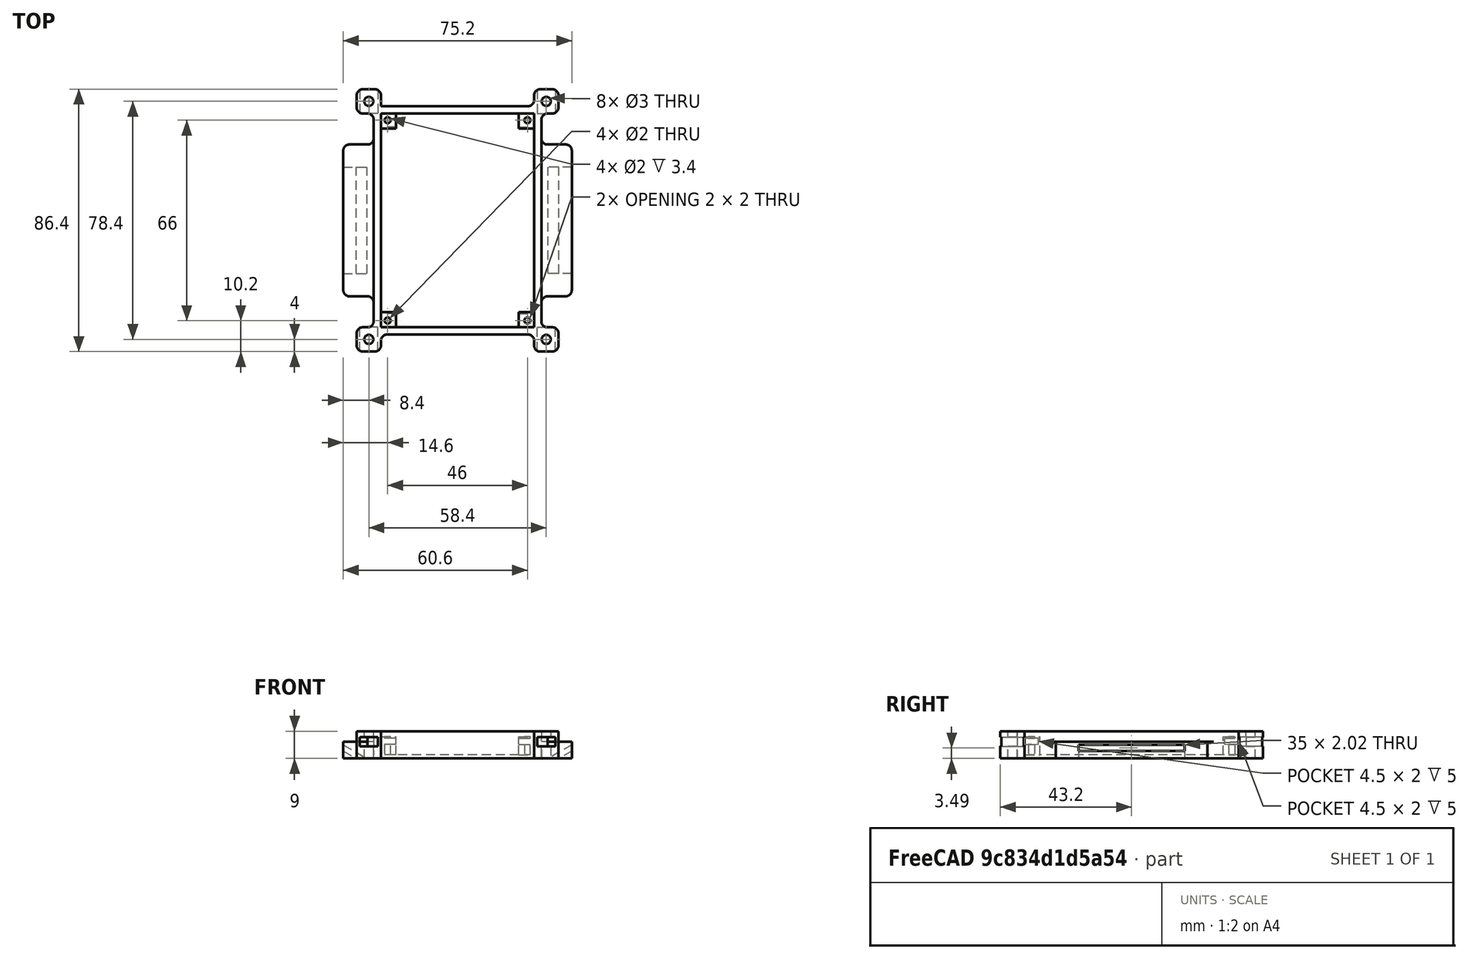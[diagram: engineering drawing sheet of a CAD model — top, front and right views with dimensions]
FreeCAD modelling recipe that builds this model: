
FCSTD DOCUMENT  (FreeCAD 0.20R29410 (Git))
Label: baseplate-2
License: All rights reserved
LicenseURL: http://en.wikipedia.org/wiki/All_rights_reserved
objects: Sketcher::SketchObject×12, PartDesign::Pad×6, PartDesign::Pocket×5, PartDesign::Fillet×3, PartDesign::Mirrored×2, Spreadsheet::Sheet×1, PartDesign::Body×1
note: 43 computed .brp shape members not serialized (recipe doc carries the construction recipe); baked Part::Feature solids carry a one-line shape summary decoded from their .brp

FEATURE [Sketcher::SketchObject] Sketch
  FullyConstrained = true
  MapMode = 5
  Support = -> [XY_Plane]
  expr: Constraints[34] = 50 + Spreadsheet.clc * 2
  expr: Constraints[35] = 70 + Spreadsheet.clc * 2
  expr: Constraints[46] = 50 + 2 * Spreadsheet.clc + 2 * Spreadsheet.thk
  expr: Constraints[47] = 70 + 2 * Spreadsheet.clc + 2 * Spreadsheet.thk
  sketch-geometry (35):
    g0: LineSegment StartX=25 StartY=35 StartZ=0 EndX=25 EndY=-35 EndZ=0
    g1: LineSegment StartX=25 StartY=-35 StartZ=0 EndX=-25 EndY=-35 EndZ=0
    g2: LineSegment StartX=-25 StartY=-35 StartZ=0 EndX=-25 EndY=35 EndZ=0
    g3: LineSegment StartX=-25 StartY=35 StartZ=0 EndX=25 EndY=35 EndZ=0
    g4: GeomPoint X=0 Y=0 Z=0
    g5: Circle CenterX=-23 CenterY=33 CenterZ=0 NormalX=0 NormalY=0 NormalZ=1 AngleXU=0 Radius=1
    g6: Circle CenterX=23 CenterY=33 CenterZ=0 NormalX=0 NormalY=0 NormalZ=1 AngleXU=0 Radius=1
    g7: Circle CenterX=23 CenterY=-33 CenterZ=0 NormalX=0 NormalY=0 NormalZ=1 AngleXU=0 Radius=1
    g8: Circle CenterX=-23 CenterY=-33 CenterZ=0 NormalX=0 NormalY=0 NormalZ=1 AngleXU=0 Radius=1
    g9: LineSegment StartX=-25.2 StartY=-35.2 StartZ=0 EndX=-25.2 EndY=35.2 EndZ=0
    g10: LineSegment StartX=-25.2 StartY=35.2 StartZ=0 EndX=25.2 EndY=35.2 EndZ=0
    g11: LineSegment StartX=25.2 StartY=35.2 StartZ=0 EndX=25.2 EndY=-35.2 EndZ=0
    g12: LineSegment StartX=25.2 StartY=-35.2 StartZ=0 EndX=-25.2 EndY=-35.2 EndZ=0
    g13: GeomPoint X=0 Y=0 Z=0
    g14: LineSegment StartX=-27.6 StartY=37.6 StartZ=0 EndX=-27.6 EndY=-37.6 EndZ=0
    g15: LineSegment StartX=-27.6 StartY=-37.6 StartZ=0 EndX=27.6 EndY=-37.6 EndZ=0
    g16: LineSegment StartX=27.6 StartY=-37.6 StartZ=0 EndX=27.6 EndY=37.6 EndZ=0
    g17: LineSegment StartX=27.6 StartY=37.6 StartZ=0 EndX=-27.6 EndY=37.6 EndZ=0
    g18: GeomPoint X=0 Y=0 Z=0
    g19: LineSegment StartX=25.2 StartY=35.2 StartZ=0 EndX=20.2 EndY=35.2 EndZ=0
    g20: LineSegment StartX=20.2 StartY=35.2 StartZ=0 EndX=20.2 EndY=30.2 EndZ=0
    g21: LineSegment StartX=20.2 StartY=30.2 StartZ=0 EndX=25.2 EndY=30.2 EndZ=0
    g22: LineSegment StartX=25.2 StartY=30.2 StartZ=0 EndX=25.2 EndY=35.2 EndZ=0
    g23: LineSegment StartX=25.2 StartY=-35.2 StartZ=0 EndX=20.2 EndY=-35.2 EndZ=0
    g24: LineSegment StartX=20.2 StartY=-35.2 StartZ=0 EndX=20.2 EndY=-30.2 EndZ=0
    g25: LineSegment StartX=20.2 StartY=-30.2 StartZ=0 EndX=25.2 EndY=-30.2 EndZ=0
    g26: LineSegment StartX=25.2 StartY=-30.2 StartZ=0 EndX=25.2 EndY=-35.2 EndZ=0
    g27: LineSegment StartX=-25.2 StartY=-35.2 StartZ=0 EndX=-20.2 EndY=-35.2 EndZ=0
    g28: LineSegment StartX=-20.2 StartY=-35.2 StartZ=0 EndX=-20.2 EndY=-30.2 EndZ=0
    g29: LineSegment StartX=-20.2 StartY=-30.2 StartZ=0 EndX=-25.2 EndY=-30.2 EndZ=0
    g30: LineSegment StartX=-25.2 StartY=-30.2 StartZ=0 EndX=-25.2 EndY=-35.2 EndZ=0
    g31: LineSegment StartX=-25.2 StartY=35.2 StartZ=0 EndX=-20.2 EndY=35.2 EndZ=0
    g32: LineSegment StartX=-20.2 StartY=35.2 StartZ=0 EndX=-20.2 EndY=30.2 EndZ=0
    g33: LineSegment StartX=-20.2 StartY=30.2 StartZ=0 EndX=-25.2 EndY=30.2 EndZ=0
    g34: LineSegment StartX=-25.2 StartY=30.2 StartZ=0 EndX=-25.2 EndY=35.2 EndZ=0
  constraints (92):
    c: Coincident(g0,g1)
    c: Coincident(g1,g2)
    c: Coincident(g2,g3)
    c: Coincident(g3,g0)
    c: Horizontal(g1)
    c: Horizontal(g3)
    c: Vertical(g0)
    c: Vertical(g2)
    c: Symmetric(g1,g0,g4)
    c: Coincident(g4,g-1)
    c: Diameter(g5) = 2
    c: Equal(g5,g6)
    c: Equal(g6,g7)
    c: Equal(g7,g8)
    c: DistanceX(g2,g5) = 2
    c: DistanceY(g5,g2) = 2
    c: DistanceY(g0,g7) = 2
    c: DistanceX(g7,g0) = 2
    c: Horizontal(g8,g7)
    c: Horizontal(g6,g5)
    c: Vertical(g8,g5)
    c: Vertical(g7,g6)
    c: DistanceX(g3,g3) = 50
    c: DistanceY(g2,g2) = 70
    c: Coincident(g9,g10)
    c: Coincident(g10,g11)
    c: Coincident(g11,g12)
    c: Coincident(g12,g9)
    c: Horizontal(g10)
    c: Horizontal(g12)
    c: Vertical(g9)
    c: Vertical(g11)
    c: Symmetric(g10,g9,g13)
    c: Coincident(g13,g4)
    c: DistanceX(g10,g10) = 50.4
    c: DistanceY(g11,g11) = 70.4
    c: Coincident(g14,g15)
    c: Coincident(g15,g16)
    c: Coincident(g16,g17)
    c: Coincident(g17,g14)
    c: Horizontal(g15)
    c: Horizontal(g17)
    c: Vertical(g14)
    c: Vertical(g16)
    c: Symmetric(g15,g14,g18)
    c: Coincident(g18,g4)
    c: DistanceX(g17,g17) = 55.2
    c: DistanceY(g16,g16) = 75.2
    c: Coincident(g19,g20)
    c: Coincident(g20,g21)
    c: Coincident(g21,g22)
    c: Coincident(g22,g19)
    c: Horizontal(g19)
    c: Horizontal(g21)
    c: Vertical(g20)
    c: Vertical(g22)
    c: Coincident(g19,g10)
    c: DistanceY(g20,g20) = 5
    c: Coincident(g23,g24)
    c: Coincident(g24,g25)
    c: Coincident(g25,g26)
    c: Coincident(g26,g23)
    c: Horizontal(g23)
    c: Horizontal(g25)
    c: Vertical(g24)
    c: Vertical(g26)
    c: Coincident(g23,g11)
    c: Coincident(g27,g28)
    c: Coincident(g28,g29)
    c: Coincident(g29,g30)
    c: Coincident(g30,g27)
    c: Horizontal(g27)
    c: Horizontal(g29)
    c: Vertical(g28)
    c: Vertical(g30)
    c: Coincident(g27,g9)
    c: Coincident(g31,g32)
    c: Coincident(g32,g33)
    c: Coincident(g33,g34)
    c: Coincident(g34,g31)
    c: Horizontal(g31)
    c: Horizontal(g33)
    c: Vertical(g32)
    c: Vertical(g34)
    c: Coincident(g31,g9)
    c: Equal(g21,g20)
    c: Equal(g33,g32)
    c: Equal(g32,g29)
    c: Equal(g29,g28)
    c: Equal(g28,g24)
    c: Equal(g24,g25)
    c: Equal(g32,g21)
FEATURE [Spreadsheet::Sheet] Spreadsheet
  cells = A1=clearance; B1(clc)=0.2; A2=thk; B2(thk)=2.4
FEATURE [PartDesign::Pad] Pad
  Direction = (0,0,1)
  Length = 1.2
  Length2 = 10
  Profile = -> Sketch
  ReferenceAxis = -> Sketch [N_Axis]
  Type = 0
  expr: Length = Spreadsheet.thk / 2
FEATURE [Sketcher::SketchObject] Sketch001
  FullyConstrained = true
  MapMode = 5
  Placement = pos=(0,0,1.2) rot=(0,0,1;0rad)
  Support = -> [Pad]
  expr: Constraints[1] = Sketch.Constraints[10]
  expr: Constraints[24] = Sketch.Constraints[46]
  expr: Constraints[25] = Sketch.Constraints[47]
  expr: Constraints[29] = Sketch.Constraints[57]
  expr: Constraints[50] = Spreadsheet.thk
  expr: Constraints[51] = Spreadsheet.thk
  expr: Constraints[52] = Spreadsheet.thk
  expr: Constraints[53] = Spreadsheet.thk
  expr: Constraints[56] = 2.8mm
  sketch-geometry (23):
    g0: GeomPoint X=0 Y=0 Z=0
    g1: Circle CenterX=-23 CenterY=33 CenterZ=0 NormalX=0 NormalY=0 NormalZ=1 AngleXU=0 Radius=1
    g2: Circle CenterX=23 CenterY=33 CenterZ=0 NormalX=0 NormalY=0 NormalZ=1 AngleXU=0 Radius=1
    g3: Circle CenterX=23 CenterY=-33 CenterZ=0 NormalX=0 NormalY=0 NormalZ=1 AngleXU=0 Radius=1
    g4: Circle CenterX=-23 CenterY=-33 CenterZ=0 NormalX=0 NormalY=0 NormalZ=1 AngleXU=0 Radius=1
    g5: LineSegment StartX=-25.2 StartY=-30.2 StartZ=0 EndX=-25.2 EndY=30.2 EndZ=0
    g6: LineSegment StartX=-20.2 StartY=35.2 StartZ=0 EndX=20.2 EndY=35.2 EndZ=0
    g7: LineSegment StartX=25.2 StartY=30.2 StartZ=0 EndX=25.2 EndY=-30.2 EndZ=0
    g8: LineSegment StartX=20.2 StartY=-35.2 StartZ=0 EndX=-20.2 EndY=-35.2 EndZ=0
    g9: GeomPoint X=0 Y=0 Z=0
    g10: LineSegment StartX=-27.6 StartY=37.6 StartZ=0 EndX=-27.6 EndY=-37.6 EndZ=0
    g11: LineSegment StartX=-27.6 StartY=-37.6 StartZ=0 EndX=27.6 EndY=-37.6 EndZ=0
    g12: LineSegment StartX=27.6 StartY=-37.6 StartZ=0 EndX=27.6 EndY=37.6 EndZ=0
    g13: LineSegment StartX=27.6 StartY=37.6 StartZ=0 EndX=-27.6 EndY=37.6 EndZ=0
    g14: GeomPoint X=0 Y=0 Z=0
    g15: LineSegment StartX=20.2 StartY=35.2 StartZ=0 EndX=20.2 EndY=30.2 EndZ=0
    g16: LineSegment StartX=20.2 StartY=30.2 StartZ=0 EndX=25.2 EndY=30.2 EndZ=0
    g17: LineSegment StartX=20.2 StartY=-35.2 StartZ=0 EndX=20.2 EndY=-30.2 EndZ=0
    g18: LineSegment StartX=20.2 StartY=-30.2 StartZ=0 EndX=25.2 EndY=-30.2 EndZ=0
    g19: LineSegment StartX=-20.2 StartY=-35.2 StartZ=0 EndX=-20.2 EndY=-30.2 EndZ=0
    g20: LineSegment StartX=-20.2 StartY=-30.2 StartZ=0 EndX=-25.2 EndY=-30.2 EndZ=0
    g21: LineSegment StartX=-20.2 StartY=35.2 StartZ=0 EndX=-20.2 EndY=30.2 EndZ=0
    g22: LineSegment StartX=-20.2 StartY=30.2 StartZ=0 EndX=-25.2 EndY=30.2 EndZ=0
  constraints (68):
    c: Coincident(g0,g-1)
    c: Diameter(g1) = 2
    c: Equal(g1,g2)
    c: Equal(g2,g3)
    c: Equal(g3,g4)
    c: Horizontal(g4,g3)
    c: Horizontal(g2,g1)
    c: Vertical(g4,g1)
    c: Vertical(g3,g2)
    c: Horizontal(g6)
    c: Horizontal(g8)
    c: Vertical(g5)
    c: Vertical(g7)
    c: Coincident(g9,g0)
    c: Coincident(g10,g11)
    c: Coincident(g11,g12)
    c: Coincident(g12,g13)
    c: Coincident(g13,g10)
    c: Horizontal(g11)
    c: Horizontal(g13)
    c: Vertical(g10)
    c: Vertical(g12)
    c: Symmetric(g11,g10,g14)
    c: Coincident(g14,g0)
    c: DistanceX(g13,g13) = 55.2
    c: DistanceY(g12,g12) = 75.2
    c: Coincident(g15,g16)
    c: Horizontal(g16)
    c: Vertical(g15)
    c: DistanceY(g15,g15) = 5
    c: Coincident(g17,g18)
    c: Horizontal(g18)
    c: Vertical(g17)
    c: Coincident(g19,g20)
    c: Horizontal(g20)
    c: Vertical(g19)
    c: Coincident(g21,g22)
    c: Horizontal(g22)
    c: Vertical(g21)
    c: Equal(g16,g15)
    c: Equal(g22,g21)
    c: Equal(g21,g20)
    c: Equal(g20,g19)
    c: Equal(g19,g17)
    c: Equal(g17,g18)
    c: Equal(g21,g16)
    c: PointOnObject(g7,g18)
    c: PointOnObject(g5,g20)
    c: PointOnObject(g5,g22)
    c: PointOnObject(g7,g16)
    c: DistanceY(g11,g8) = 2.4
    c: DistanceX(g7,g11) = 2.4
    c: DistanceX(g10,g5) = 2.4
    c: DistanceY(g6,g10) = 2.4
    c: Equal(g6,g8)
    c: Equal(g7,g5)
    c: DistanceX(g6,g2) = 2.8
    c: DistanceY(g15,g2) = 2.8
    c: DistanceY(g8,g4) = 2.2
    c: DistanceX(g5,g4) = 2.2
    c: DistanceX(g10,g21) = 7.4
    c: DistanceX(g17,g11) = 7.4
    c: DistanceY(g21,g10) = 7.4
    c: DistanceX(g6,g12) = 7.4
    c: DistanceX(g10,g19) = 7.4
    c: Coincident(g8,g17)
    c: Coincident(g8,g19)
    c: Coincident(g16,g7)
FEATURE [PartDesign::Pad] Pad001
  BaseFeature = -> Pad
  Direction = (0,0,1)
  Length = 6
  Length2 = 10
  Profile = -> Sketch001
  ReferenceAxis = -> Sketch001 [N_Axis]
  Type = 0
FEATURE [Sketcher::SketchObject] Sketch002
  ExternalGeometry = -> [Pad001]
  FullyConstrained = true
  MapMode = 5
  Placement = pos=(0,0,7.2) rot=(0,0,1;0rad)
  Support = -> [Pad001]
  expr: Constraints[20] = 50 + Spreadsheet.clc * 2
  expr: Constraints[21] = 70 + Spreadsheet.clc * 2
  sketch-geometry (9):
    g0: LineSegment StartX=-27.6 StartY=37.6 StartZ=0 EndX=27.6 EndY=37.6 EndZ=0
    g1: LineSegment StartX=27.6 StartY=37.6 StartZ=0 EndX=27.6 EndY=-37.6 EndZ=0
    g2: LineSegment StartX=27.6 StartY=-37.6 StartZ=0 EndX=-27.6 EndY=-37.6 EndZ=0
    g3: LineSegment StartX=-27.6 StartY=-37.6 StartZ=0 EndX=-27.6 EndY=37.6 EndZ=0
    g4: LineSegment StartX=-25.2 StartY=35.2 StartZ=0 EndX=-25.2 EndY=-35.2 EndZ=0
    g5: LineSegment StartX=-25.2 StartY=-35.2 StartZ=0 EndX=25.2 EndY=-35.2 EndZ=0
    g6: LineSegment StartX=25.2 StartY=-35.2 StartZ=0 EndX=25.2 EndY=35.2 EndZ=0
    g7: LineSegment StartX=25.2 StartY=35.2 StartZ=0 EndX=-25.2 EndY=35.2 EndZ=0
    g8: GeomPoint X=0 Y=0 Z=0
  constraints (22):
    c: Coincident(g0,g1)
    c: Coincident(g1,g2)
    c: Coincident(g2,g3)
    c: Coincident(g3,g0)
    c: Horizontal(g0)
    c: Horizontal(g2)
    c: Vertical(g1)
    c: Vertical(g3)
    c: Coincident(g0,g-3)
    c: Coincident(g1,g-4)
    c: Coincident(g4,g5)
    c: Coincident(g5,g6)
    c: Coincident(g6,g7)
    c: Coincident(g7,g4)
    c: Horizontal(g5)
    c: Horizontal(g7)
    c: Vertical(g4)
    c: Vertical(g6)
    c: Symmetric(g5,g4,g8)
    c: Coincident(g8,g-1)
    c: DistanceX(g7,g7) = 50.4
    c: DistanceY(g6,g6) = 70.4
FEATURE [PartDesign::Pad] Pad002
  BaseFeature = -> Pad001
  Direction = (0,0,1)
  Length = 9.8
  Length2 = 10
  Profile = -> Sketch002
  ReferenceAxis = -> Sketch002 [N_Axis]
  Type = 0
FEATURE [Sketcher::SketchObject] Sketch003
  ExternalGeometry = -> [Pad002]
  FullyConstrained = true
  MapMode = 5
  Placement = pos=(0,0,17) rot=(0,0,1;0rad)
  Support = -> [Pad002]
  sketch-geometry (16):
    g0: LineSegment StartX=25.2 StartY=-35.2 StartZ=0 EndX=33.2 EndY=-35.2 EndZ=0
    g1: LineSegment StartX=33.2 StartY=-35.2 StartZ=0 EndX=33.2 EndY=-43.2 EndZ=0
    g2: LineSegment StartX=33.2 StartY=-43.2 StartZ=0 EndX=25.2 EndY=-43.2 EndZ=0
    g3: LineSegment StartX=25.2 StartY=-43.2 StartZ=0 EndX=25.2 EndY=-35.2 EndZ=0
    g4: LineSegment StartX=-25.2 StartY=-35.2 StartZ=0 EndX=-33.2 EndY=-35.2 EndZ=0
    g5: LineSegment StartX=-33.2 StartY=-35.2 StartZ=0 EndX=-33.2 EndY=-43.2 EndZ=0
    g6: LineSegment StartX=-33.2 StartY=-43.2 StartZ=0 EndX=-25.2 EndY=-43.2 EndZ=0
    g7: LineSegment StartX=-25.2 StartY=-43.2 StartZ=0 EndX=-25.2 EndY=-35.2 EndZ=0
    g8: LineSegment StartX=-25.2 StartY=35.2 StartZ=0 EndX=-33.2 EndY=35.2 EndZ=0
    g9: LineSegment StartX=-33.2 StartY=35.2 StartZ=0 EndX=-33.2 EndY=43.2 EndZ=0
    g10: LineSegment StartX=-33.2 StartY=43.2 StartZ=0 EndX=-25.2 EndY=43.2 EndZ=0
    g11: LineSegment StartX=-25.2 StartY=43.2 StartZ=0 EndX=-25.2 EndY=35.2 EndZ=0
    g12: LineSegment StartX=25.2 StartY=35.2 StartZ=0 EndX=33.2 EndY=35.2 EndZ=0
    g13: LineSegment StartX=33.2 StartY=35.2 StartZ=0 EndX=33.2 EndY=43.2 EndZ=0
    g14: LineSegment StartX=33.2 StartY=43.2 StartZ=0 EndX=25.2 EndY=43.2 EndZ=0
    g15: LineSegment StartX=25.2 StartY=43.2 StartZ=0 EndX=25.2 EndY=35.2 EndZ=0
  constraints (44):
    c: Coincident(g0,g1)
    c: Coincident(g1,g2)
    c: Coincident(g2,g3)
    c: Coincident(g3,g0)
    c: Horizontal(g0)
    c: Horizontal(g2)
    c: Vertical(g1)
    c: Vertical(g3)
    c: Coincident(g0,g-6)
    c: Coincident(g4,g5)
    c: Coincident(g5,g6)
    c: Coincident(g6,g7)
    c: Coincident(g7,g4)
    c: Horizontal(g4)
    c: Horizontal(g6)
    c: Vertical(g5)
    c: Vertical(g7)
    c: Coincident(g4,g-5)
    c: Coincident(g8,g9)
    c: Coincident(g9,g10)
    c: Coincident(g10,g11)
    c: Coincident(g11,g8)
    c: Horizontal(g8)
    c: Horizontal(g10)
    c: Vertical(g9)
    c: Vertical(g11)
    c: Coincident(g8,g-4)
    c: Coincident(g12,g13)
    c: Coincident(g13,g14)
    c: Coincident(g14,g15)
    c: Coincident(g15,g12)
    c: Horizontal(g12)
    c: Horizontal(g14)
    c: Vertical(g13)
    c: Vertical(g15)
    c: Coincident(g12,g-3)
    c: Equal(g10,g9)
    c: Equal(g9,g14)
    c: Equal(g14,g13)
    c: Equal(g13,g1)
    c: Equal(g1,g2)
    c: Equal(g2,g6)
    c: Equal(g6,g5)
    c: DistanceY(g13,g13) = 8
FEATURE [PartDesign::Pad] Pad003
  BaseFeature = -> Pad002
  Direction = (0,0,1)
  Length = 10
  Length2 = 10
  Profile = -> Sketch003
  ReferenceAxis = -> Sketch003 [N_Axis]
  Reversed = true
  Type = 3
  UpToFace = -> Pad002 [Face4]
FEATURE [PartDesign::Fillet] Fillet
  Base = -> Pad003 [Edge79,Edge78,Edge41,Edge21,Edge20,Edge27,Edge51,Edge53,Edge33,Edge60,Edge102,Edge65,Edge67,Edge66,Edge71,Edge69,Edge73,Edge38,Edge108,Edge80,Edge84,Edge82,Edge43,Edge86,Edge114,Edge91,Edge54,Edge57,Edge46,Edge30,Edge29,Edge28]
  BaseFeature = -> Pad003
  Radius = 2
  SupportTransform = false
  UseAllEdges = false
  expr: Radius = 2
FEATURE [Sketcher::SketchObject] Sketch004
  ExternalGeometry = -> [Fillet]
  FullyConstrained = true
  MapMode = 5
  Placement = pos=(-20.2,0,0) rot=(0.57735,0.57735,0.57735;2.0944rad)
  Support = -> [Fillet]
  sketch-geometry (8):
    g0: LineSegment StartX=30.7 StartY=6.6 StartZ=0 EndX=35.2 EndY=6.6 EndZ=0
    g1: LineSegment StartX=35.2 StartY=6.6 StartZ=0 EndX=35.2 EndY=4.6 EndZ=0
    g2: LineSegment StartX=35.2 StartY=4.6 StartZ=0 EndX=30.7 EndY=4.6 EndZ=0
    g3: LineSegment StartX=30.7 StartY=4.6 StartZ=0 EndX=30.7 EndY=6.6 EndZ=0
    g4: LineSegment StartX=-30.7 StartY=6.6 StartZ=0 EndX=-35.2 EndY=6.6 EndZ=0
    g5: LineSegment StartX=-35.2 StartY=6.6 StartZ=0 EndX=-35.2 EndY=4.6 EndZ=0
    g6: LineSegment StartX=-35.2 StartY=4.6 StartZ=0 EndX=-30.7 EndY=4.6 EndZ=0
    g7: LineSegment StartX=-30.7 StartY=4.6 StartZ=0 EndX=-30.7 EndY=6.6 EndZ=0
  constraints (24):
    c: Coincident(g0,g1)
    c: Coincident(g1,g2)
    c: Coincident(g2,g3)
    c: Coincident(g3,g0)
    c: Horizontal(g0)
    c: Horizontal(g2)
    c: Vertical(g1)
    c: Vertical(g3)
    c: DistanceY(g3,g3) = 2
    c: DistanceX(g0,g0) = 4.5
    c: DistanceX(g-3,g0) = 0.5
    c: Coincident(g4,g5)
    c: Coincident(g5,g6)
    c: Coincident(g6,g7)
    c: Coincident(g7,g4)
    c: Horizontal(g4)
    c: Horizontal(g6)
    c: Vertical(g5)
    c: Vertical(g7)
    c: DistanceX(g4,g4) = 4.5
    c: DistanceX(g4,g-4) = 0.5
    c: DistanceY(g7,g7) = 2
    c: PointOnObject(g2,g6)
    c: DistanceY(g4,g-4) = 0.6
FEATURE [PartDesign::Pocket] Pocket
  BaseFeature = -> Fillet
  Direction = (-1,0,0)
  Length = 0
  Length2 = 5
  Profile = -> Sketch004
  ReferenceAxis = -> Sketch004 [N_Axis]
  Type = 3
  UpToFace = -> Fillet [Face85]
FEATURE [PartDesign::Mirrored] Mirrored
  BaseFeature = -> Pocket
  MirrorPlane = -> YZ_Plane
  Originals = -> [Pocket]
FEATURE [Sketcher::SketchObject] Sketch005
  FullyConstrained = true
  MapMode = 5
  Placement = pos=(0,-43.2,0) rot=(1,0,0;1.5708rad)
  Support = -> [Mirrored]
FEATURE [Sketcher::SketchObject] Sketch006
  ExternalGeometry = -> [Mirrored]
  FullyConstrained = false
  MapMode = 5
  Placement = pos=(0,0,17) rot=(0,0,1;0rad)
  Support = -> [Mirrored]
  sketch-geometry (8):
    g0: Circle CenterX=-29.2 CenterY=39.2 CenterZ=0 NormalX=0 NormalY=0 NormalZ=1 AngleXU=0 Radius=1.5
    g1: Circle CenterX=29.2 CenterY=39.2 CenterZ=0 NormalX=0 NormalY=0 NormalZ=1 AngleXU=0 Radius=1.5
    g2: Circle CenterX=29.2 CenterY=-39.2 CenterZ=0 NormalX=0 NormalY=0 NormalZ=1 AngleXU=0 Radius=1.5
    g3: Circle CenterX=-29.2 CenterY=-39.2 CenterZ=0 NormalX=0 NormalY=0 NormalZ=1 AngleXU=0 Radius=1.5
    g4: LineSegment StartX=29.2 StartY=-39.2 StartZ=0 EndX=29.2 EndY=-42.1749 EndZ=0
    g5: LineSegment StartX=29.2 StartY=-39.2 StartZ=0 EndX=32.2991 EndY=-39.2 EndZ=0
    g6: LineSegment StartX=-29.2 StartY=39.2 StartZ=0 EndX=-29.2 EndY=42.4001 EndZ=0
    g7: LineSegment StartX=-29.2 StartY=39.2 StartZ=0 EndX=-32.1259 EndY=39.2 EndZ=0
  constraints (16):
    c: Equal(g0,g1)
    c: Equal(g1,g2)
    c: Equal(g2,g3)
    c: Diameter(g0) = 3
    c: Coincident(g4,g2)
    c: Symmetric(g-5,g-5,g4)
    c: Symmetric(g-6,g-6,g5)
    c: Coincident(g2,g5)
    c: Coincident(g6,g0)
    c: Coincident(g7,g0)
    c: Symmetric(g-3,g-3,g6)
    c: Symmetric(g-4,g-4,g7)
    c: Horizontal(g1,g0)
    c: Horizontal(g2,g3)
    c: Vertical(g3,g0)
    c: Vertical(g1,g2)
FEATURE [PartDesign::Pocket] Pocket001
  BaseFeature = -> Mirrored
  Direction = (0,0,-1)
  Length = 5
  Length2 = 5
  Profile = -> Sketch006
  ReferenceAxis = -> Sketch006 [N_Axis]
  Type = 1
FEATURE [Sketcher::SketchObject] Sketch007
  ExternalGeometry = -> [Pocket001]
  FullyConstrained = false
  MapMode = 5
  Placement = pos=(0,-43.2,0) rot=(1,0,0;1.5708rad)
  Support = -> [Pocket001]
  sketch-geometry (12):
    g0: LineSegment StartX=-26.2 StartY=15 StartZ=0 EndX=-26.2 EndY=12 EndZ=0
    g1: LineSegment StartX=-26.2 StartY=12 StartZ=0 EndX=-32.2 EndY=12 EndZ=0
    g2: LineSegment StartX=-32.2 StartY=12 StartZ=0 EndX=-32.2 EndY=15 EndZ=0
    g3: LineSegment StartX=-32.2 StartY=15 StartZ=0 EndX=-26.2 EndY=15 EndZ=0
    g4: GeomPoint X=-29.2 Y=13.5 Z=0
    g5: LineSegment StartX=-29.2 StartY=12 StartZ=0 EndX=-29.2 EndY=1.21098 EndZ=0
    g6: LineSegment StartX=26.2 StartY=15 StartZ=0 EndX=26.2 EndY=12 EndZ=0
    g7: LineSegment StartX=26.2 StartY=12 StartZ=0 EndX=32.2 EndY=12 EndZ=0
    g8: LineSegment StartX=32.2 StartY=12 StartZ=0 EndX=32.2 EndY=15 EndZ=0
    g9: LineSegment StartX=32.2 StartY=15 StartZ=0 EndX=26.2 EndY=15 EndZ=0
    g10: GeomPoint X=29.2 Y=13.5 Z=0
    g11: LineSegment StartX=29.2 StartY=12 StartZ=0 EndX=29.2 EndY=1.80333 EndZ=0
  constraints (28):
    c: Coincident(g0,g1)
    c: Coincident(g1,g2)
    c: Coincident(g2,g3)
    c: Coincident(g3,g0)
    c: Horizontal(g3)
    c: Vertical(g0)
    c: Vertical(g2)
    c: Symmetric(g1,g0,g4)
    c: DistanceX(g1,g1) = 6
    c: DistanceY(g2,g2) = 3
    c: PointOnObject(g5,g1)
    c: Symmetric(g0,g1,g5)
    c: Symmetric(g-3,g-3,g5)
    c: DistanceY(g2,g-3) = 2
    c: Coincident(g6,g7)
    c: Coincident(g7,g8)
    c: Coincident(g8,g9)
    c: Coincident(g9,g6)
    c: Horizontal(g9)
    c: Vertical(g6)
    c: Vertical(g8)
    c: Symmetric(g7,g6,g10)
    c: PointOnObject(g0,g9)
    c: Equal(g0,g6)
    c: Equal(g7,g1)
    c: PointOnObject(g11,g7)
    c: Symmetric(g-4,g-4,g11)
    c: Symmetric(g7,g6,g11)
FEATURE [PartDesign::Pocket] Pocket002
  BaseFeature = -> Pocket001
  Direction = (0,1,-2e-16)
  Length = 0
  Length2 = 5
  Profile = -> Sketch007
  ReferenceAxis = -> Sketch007 [N_Axis]
  Type = 3
  UpToFace = -> Pocket001 [Face51]
FEATURE [PartDesign::Mirrored] Mirrored001
  BaseFeature = -> Pocket002
  MirrorPlane = -> XZ_Plane
  Originals = -> [Pocket002]
FEATURE [Sketcher::SketchObject] Sketch008
  FullyConstrained = true
  MapMode = 5
  Placement = pos=(-27.6,0,0) rot=(0.57735,-0.57735,-0.57735;2.0944rad)
  Support = -> [Mirrored001]
  sketch-geometry (5):
    g0: LineSegment StartX=-25 StartY=5.5 StartZ=0 EndX=-25 EndY=0 EndZ=0
    g1: LineSegment StartX=-25 StartY=0 StartZ=0 EndX=25 EndY=0 EndZ=0
    g2: LineSegment StartX=25 StartY=0 StartZ=0 EndX=25 EndY=5.5 EndZ=0
    g3: LineSegment StartX=25 StartY=5.5 StartZ=0 EndX=-25 EndY=5.5 EndZ=0
    g4: GeomPoint X=0 Y=2.75 Z=0
  constraints (13):
    c: Coincident(g0,g1)
    c: Coincident(g1,g2)
    c: Coincident(g2,g3)
    c: Coincident(g3,g0)
    c: Horizontal(g1)
    c: Horizontal(g3)
    c: Vertical(g0)
    c: Vertical(g2)
    c: Symmetric(g1,g0,g4)
    c: PointOnObject(g4,g-2)
    c: PointOnObject(g1,g-1)
    c: DistanceY(g2,g2) = 5.5
    c: DistanceX(g3,g3) = 50
FEATURE [PartDesign::Pad] Pad004
  BaseFeature = -> Mirrored001
  Direction = (-1,0,0)
  Length = 10
  Length2 = 10
  Profile = -> Sketch008
  ReferenceAxis = -> Sketch008 [N_Axis]
  Type = 0
FEATURE [Sketcher::SketchObject] Sketch009
  ExternalGeometry = -> [Pad004]
  FullyConstrained = false
  MapMode = 5
  Placement = pos=(0,0,0) rot=(1,0,0;1.5708rad)
  Support = -> [XZ_Plane]
  sketch-geometry (7):
    g0: LineSegment StartX=-37.6 StartY=-6.8e-15 StartZ=0 EndX=27.6 EndY=-7.4e-15 EndZ=0
    g1: LineSegment StartX=-37.6 StartY=5.5 StartZ=0 EndX=-37.6 EndY=-7.1e-15 EndZ=0
    g2: LineSegment StartX=-37.6 StartY=2.47927 StartZ=0 EndX=-33.3058 EndY=-6.7e-15 EndZ=0
    g3: LineSegment StartX=-37.6 StartY=4.5 StartZ=0 EndX=-29.8058 EndY=-7.1e-15 EndZ=0
    g4: LineSegment StartX=-35.1293 StartY=1.05284 StartZ=0 EndX=-34.2543 EndY=2.56839 EndZ=0
    g5: LineSegment StartX=-37.6 StartY=4.5 StartZ=0 EndX=-37.6 EndY=2.47927 EndZ=0
    g6: LineSegment StartX=-33.3058 StartY=-6.8e-15 StartZ=0 EndX=-29.8058 EndY=-6.8e-15 EndZ=0
  constraints (20):
    c: Coincident(g0,g-3)
    c: Coincident(g1,g-4)
    c: Coincident(g1,g0)
    c: Vertical(g1)
    c: PointOnObject(g2,g1)
    c: PointOnObject(g2,g0)
    c: PointOnObject(g3,g1)
    c: PointOnObject(g3,g0)
    c: Parallel(g2,g3)
    c: PointOnObject(g4,g2)
    c: PointOnObject(g4,g3)
    c: Perpendicular(g3,g4)
    c: Distance(g4) = 1.75
    c: Coincident(g5,g3)
    c: Coincident(g5,g2)
    c: Coincident(g6,g2)
    c: Coincident(g6,g3)
    c: Horizontal(g6)
    c: DistanceY(g3,g1) = 1
    c: Angle(g3,g6) = 0.523599
FEATURE [PartDesign::Pocket] Pocket003
  BaseFeature = -> Pad004
  Direction = (0,1,2e-16)
  Length = 35
  Length2 = 5
  Midplane = true
  Profile = -> Sketch009
  ReferenceAxis = -> Sketch009 [N_Axis]
  Type = 0
FEATURE [PartDesign::Fillet] Fillet001
  Base = -> Pocket003 [Edge172,Edge111,Edge174,Edge122,Edge212,Edge210]
  BaseFeature = -> Pocket003
  Radius = 2
  SupportTransform = false
  UseAllEdges = false
FEATURE [Sketcher::SketchObject] Sketch010
  FullyConstrained = true
  MapMode = 5
  Placement = pos=(27.6,0,0) rot=(0.57735,0.57735,0.57735;2.0944rad)
  Support = -> [Fillet001]
  sketch-geometry (5):
    g0: LineSegment StartX=-25 StartY=5.5 StartZ=0 EndX=-25 EndY=0 EndZ=0
    g1: LineSegment StartX=-25 StartY=0 StartZ=0 EndX=25 EndY=0 EndZ=0
    g2: LineSegment StartX=25 StartY=0 StartZ=0 EndX=25 EndY=5.5 EndZ=0
    g3: LineSegment StartX=25 StartY=5.5 StartZ=0 EndX=-25 EndY=5.5 EndZ=0
    g4: GeomPoint X=0 Y=2.75 Z=0
  constraints (13):
    c: Coincident(g0,g1)
    c: Coincident(g1,g2)
    c: Coincident(g2,g3)
    c: Coincident(g3,g0)
    c: Horizontal(g1)
    c: Horizontal(g3)
    c: Vertical(g0)
    c: Vertical(g2)
    c: Symmetric(g1,g0,g4)
    c: PointOnObject(g4,g-2)
    c: DistanceY(g2,g2) = 5.5
    c: DistanceX(g3,g3) = 50
    c: PointOnObject(g1,g-1)
FEATURE [PartDesign::Pad] Pad005
  BaseFeature = -> Fillet001
  Direction = (1,0,0)
  Length = 10
  Length2 = 10
  Profile = -> Sketch010
  ReferenceAxis = -> Sketch010 [N_Axis]
  Type = 0
FEATURE [Sketcher::SketchObject] Sketch011
  ExternalGeometry = -> [Pad005]
  FullyConstrained = false
  MapMode = 5
  Placement = pos=(0,0,0) rot=(1,0,0;1.5708rad)
  Support = -> [XZ_Plane]
  sketch-geometry (7):
    g0: LineSegment StartX=27.6 StartY=-5.6e-15 StartZ=0 EndX=37.6 EndY=-5.6e-15 EndZ=0
    g1: LineSegment StartX=37.6 StartY=-5.6e-15 StartZ=0 EndX=27.2 EndY=12 EndZ=0
    g2: LineSegment StartX=28.0667 StartY=11 StartZ=0 EndX=9.01411 EndY=-5.3e-15 EndZ=0
    g3: LineSegment StartX=29.2339 StartY=9.65318 StartZ=0 EndX=12.5141 EndY=-5.3e-15 EndZ=0
    g4: LineSegment StartX=34.6198 StartY=12.7627 StartZ=0 EndX=33.7448 EndY=14.2783 EndZ=0
    g5: LineSegment StartX=28.0667 StartY=11 StartZ=0 EndX=29.2339 EndY=9.65318 EndZ=0
    g6: LineSegment StartX=12.5141 StartY=-5.6e-15 StartZ=0 EndX=9.01411 EndY=-5.6e-15 EndZ=0
  constraints (19):
    c: Coincident(g0,g-4)
    c: Coincident(g0,g-5)
    c: Coincident(g1,g0)
    c: Coincident(g1,g-3)
    c: PointOnObject(g2,g1)
    c: PointOnObject(g2,g0)
    c: PointOnObject(g3,g1)
    c: PointOnObject(g3,g0)
    c: Parallel(g2,g3)
    c: PointOnObject(g4,g3)
    c: PointOnObject(g4,g2)
    c: Perpendicular(g3,g4)
    c: Distance(g4) = 1.75
    c: Angle(g0,g2) = 0.523599
    c: DistanceY(g2,g1) = 1
    c: Coincident(g5,g2)
    c: Coincident(g5,g3)
    c: Coincident(g6,g3)
    c: Coincident(g6,g2)
FEATURE [PartDesign::Pocket] Pocket004
  BaseFeature = -> Pad005
  Direction = (0,1,2e-16)
  Length = 35
  Length2 = 5
  Midplane = true
  Profile = -> Sketch011
  ReferenceAxis = -> Sketch011 [N_Axis]
  Type = 0
FEATURE [PartDesign::Fillet] Fillet002
  Base = -> Pocket004 [Edge270,Edge264,Edge105,Edge261,Edge94,Edge262]
  BaseFeature = -> Pocket004
  Radius = 2
  SupportTransform = false
  UseAllEdges = false
FEATURE [PartDesign::Body] Body
  Group = -> [Sketch,Pad,Sketch001,Pad001,Sketch002,Pad002,Sketch003,Pad003,Fillet,Sketch004,Pocket,Mirrored,Sketch005,Sketch006,Pocket001,Sketch007,Pocket002,Mirrored001,Sketch008,Pad004,Sketch009,Pocket003,Fillet001,Sketch010,Pad005,Sketch011,Pocket004,Fillet002]
  Origin = -> Origin
  Tip = -> Fillet002
